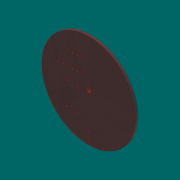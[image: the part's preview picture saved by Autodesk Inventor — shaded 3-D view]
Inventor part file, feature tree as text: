
AUTODESK INVENTOR PART (.ipt)
format: ipt  version: 2013 (Build 170138000, 138)  size: 165,376 bytes
history: native  units: mm
features: sketch x6, extrude x3, hole x3, other x1
ambient origin geometry x8: Origin, YZ Plane, XZ Plane, XY Plane, X Axis, Y Axis, Z Axis, Center Point
feature tree (13):
  other  "ソリッド1"
  extrude  "押し出し1"  Depth=200.0mm
  hole  "穴5"  [1 undecoded]
  extrude  "押し出し4"  Depth=8.0mm
  hole  "穴6"  [1 undecoded]
  extrude  "押し出し7"  Depth=12.0mm
  hole  "穴7"  [1 undecoded]
  sketch  "スケッチ1"
  sketch  "スケッチ12"
  sketch  "スケッチ13"
  sketch  "スケッチ14"
  sketch  "スケッチ16"
  sketch  "スケッチ17"
note: 3 required parameter values undecoded (feature->parameter linkage not recoverable at this tier; creation-order binding heuristic only, values carry confidence <= 0.55)
